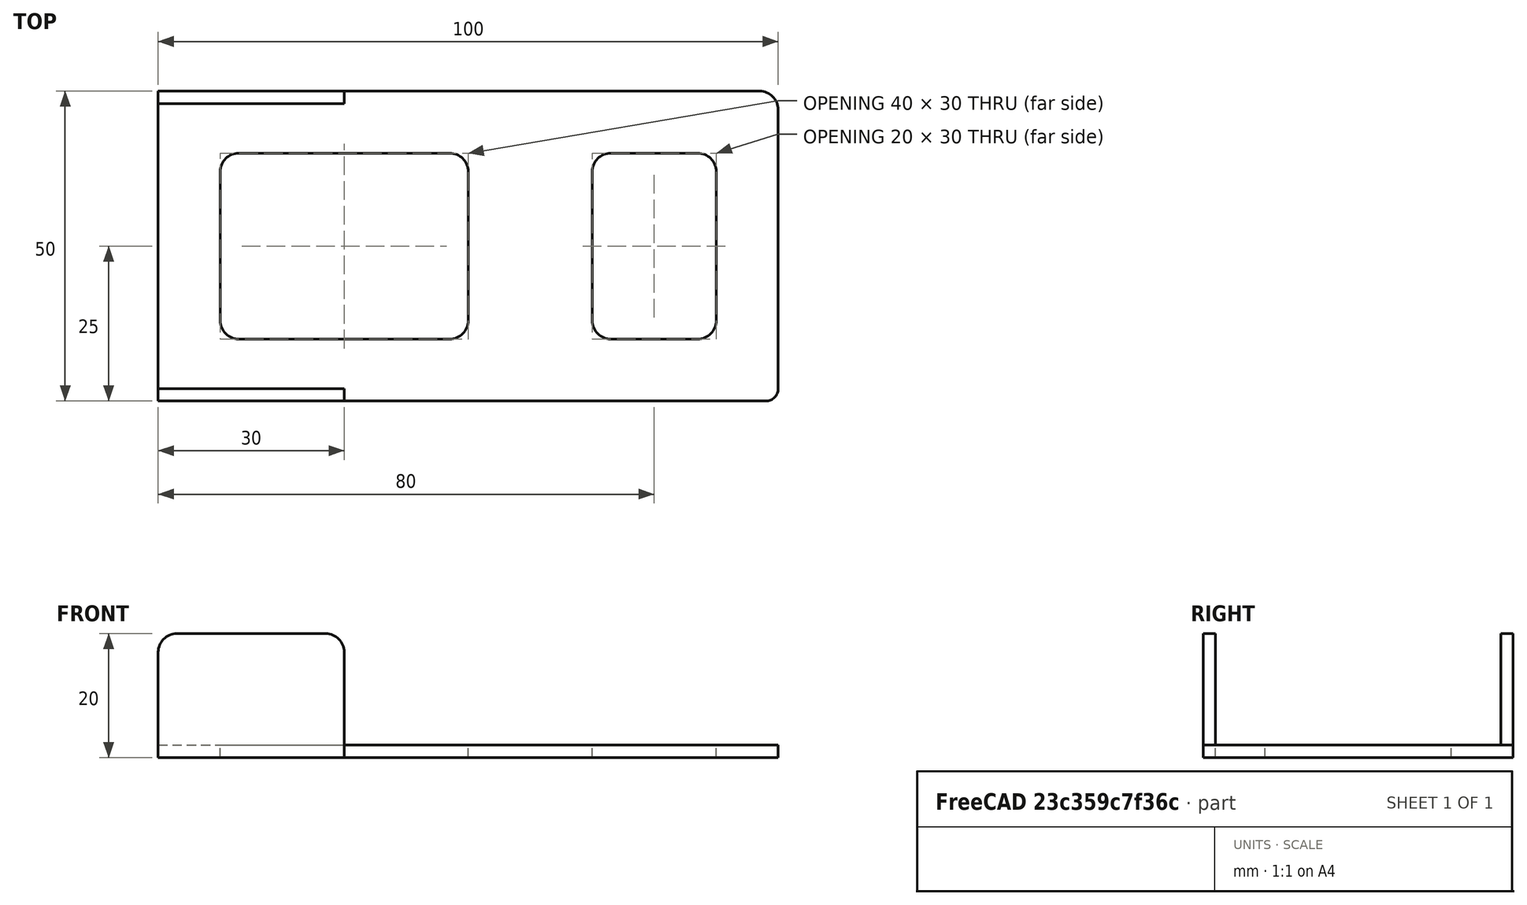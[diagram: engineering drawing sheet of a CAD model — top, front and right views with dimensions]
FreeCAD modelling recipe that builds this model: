
FCSTD DOCUMENT  (FreeCAD 0.20R29177 +426 (Git))
Label: parteRedondeada
License: All rights reserved
LicenseURL: http://en.wikipedia.org/wiki/All_rights_reserved
objects: Part::Fillet×5, Part::Box×4, Part::Cut×2, Part::FeaturePython×1, Part::MultiFuse×1
note: 12 computed .brp shape members not serialized (recipe doc carries the construction recipe); baked Part::Feature solids carry a one-line shape summary decoded from their .brp

FEATURE [Part::Box] Box  label="Cubo"
  AttacherType = Attacher::AttachEngine3D
  Height = 2
  Length = 100
  Width = 50
FEATURE [Part::Fillet] Fillet
  Base = -> Box
  Edges = 3 edges r=2: [Edge1,Edge3,Edge5]
FEATURE [Part::Fillet] Fillet001
  Base = -> Fillet
  Edges = 1 edges r=3: [Edge20]
FEATURE [Part::Box] Box001  label="Cubo001"
  AttacherType = Attacher::AttachEngine3D
  Height = 2
  Length = 40
  Placement = pos=(10,10,0) rot=(0,0,1;0rad)
  Width = 30
FEATURE [Part::Fillet] Fillet002
  Base = -> Box001
  Edges = 4 edges r=3: [Edge1,Edge3,Edge5,Edge7]
FEATURE [Part::Cut] Cut
  Base = -> Fillet001
  Refine = true
  Tool = -> Fillet002
FEATURE [Part::Box] Box002  label="Cubo002"
  AttacherType = Attacher::AttachEngine3D
  Height = 2
  Length = 20
  Width = 30
FEATURE [Part::Fillet] Fillet003
  Base = -> Box002
  Edges = 4 edges r=3: [Edge1,Edge3,Edge5,Edge7]
  Placement = pos=(70,10,0) rot=(0,0,1;0rad)
FEATURE [Part::Cut] Cut001
  Base = -> Cut
  Refine = true
  Tool = -> Fillet003
FEATURE [Part::Box] Box003  label="Cubo003"
  AttacherType = Attacher::AttachEngine3D
  Height = 20
  Length = 30
  Width = 2
FEATURE [Part::Fillet] Fillet004
  Base = -> Box003
  Edges = 2 edges r=3: [Edge2,Edge6]
FEATURE [Part::FeaturePython] Array  # Draft array (typed FeaturePython)
  AlwaysSyncPlacement = false
  Angle = 360
  ArrayType = 0
  Axis = (0,0,1)
  Base = -> Fillet004
  Center = (0,0,0)
  Count = 2
  ExpandArray = false
  Fuse = false
  IntervalAxis = (0,0,0)
  IntervalX = (50,0,0)
  IntervalY = (0,48,0)
  IntervalZ = (0,0,100)
  NumberCircles = 3
  NumberPolar = 5
  NumberX = 1
  NumberY = 2
  NumberZ = 1
  PlacementList = 2 placements: [(0,0,0),(0,48,0)]
  RadialDistance = 50
  ScaleList = (2) [(1,1,1),(1,1,1)]
  Symmetry = 1
  TangentialDistance = 25
FEATURE [Part::MultiFuse] Fusion
  Refine = true
  Shapes = -> [Array,Cut001]
